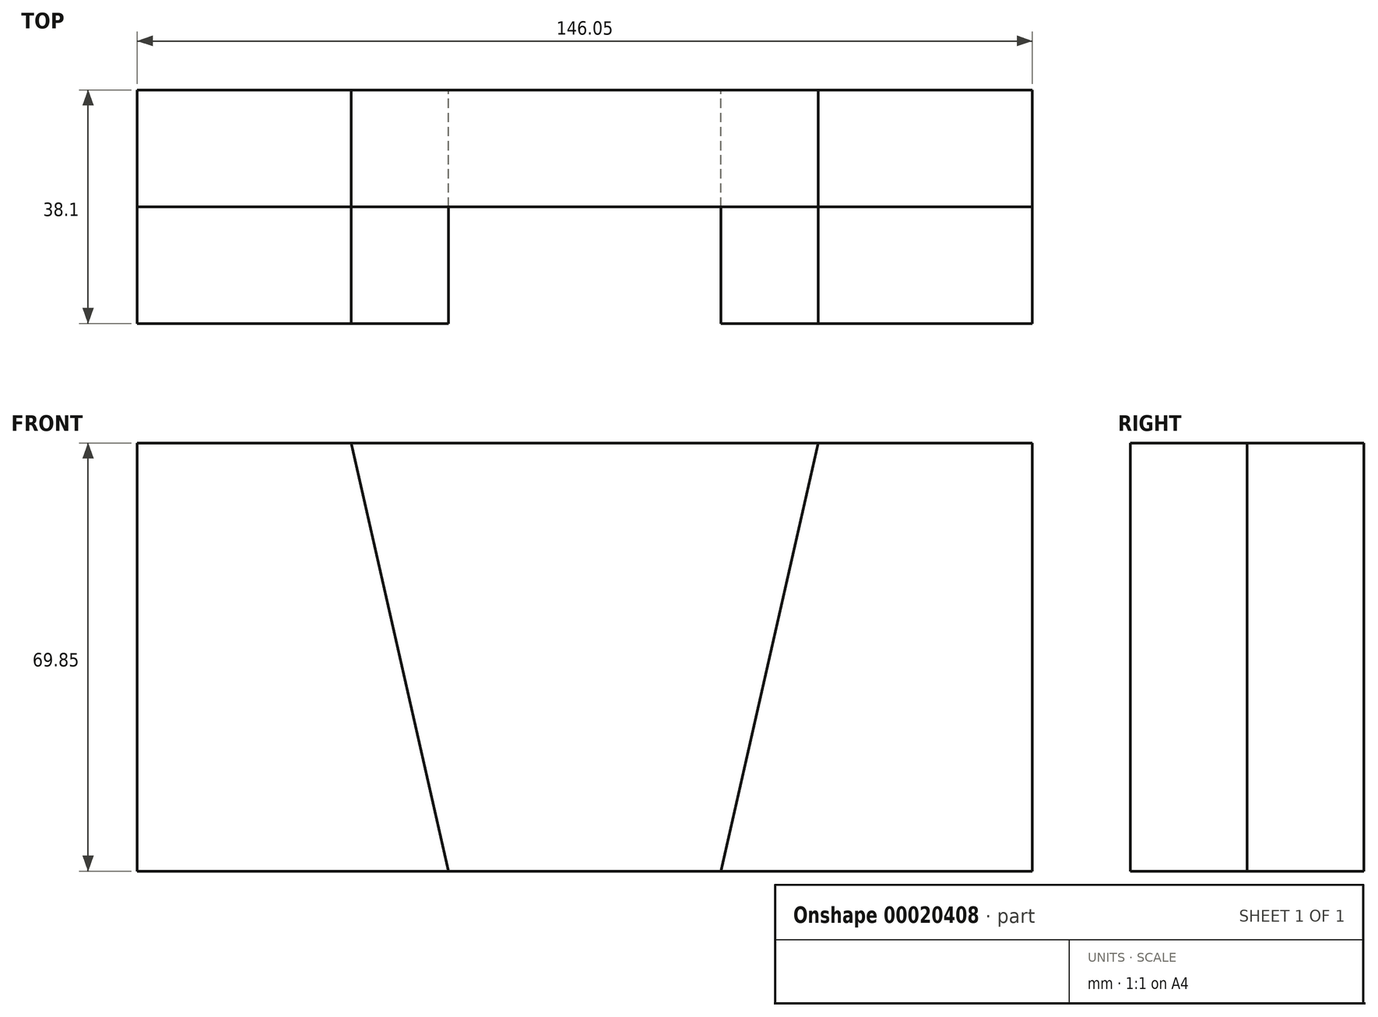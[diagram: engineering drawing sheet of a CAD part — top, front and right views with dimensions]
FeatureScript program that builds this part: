
annotation { "Feature Type Name" : "Feature", "Feature Type Description" : "" }
export const myFeature = defineFeature(function(context is Context, id is Id, definition is map)
    precondition{}
    {
        {
            var Q0;
            Q0=qCreatedBy(makeId("Front.planeOp"),FACE);
            var sketch = newSketch(context, id + "F0", { "sketchPlane" : qUnion([Q0])});
            skLineSegment(sketch, "E0.bottom", {"start": v(-72.73, 28.3) * mm, "end": v(73.32, 28.3) * mm});
            skLineSegment(sketch, "E0.top", {"start": v(-72.73, -41.55) * mm, "end": v(73.32, -41.55) * mm});
            skLineSegment(sketch, "E0.left", {"start": v(-72.73, 28.3) * mm, "end": v(-72.73, -41.55) * mm});
            skLineSegment(sketch, "E0.right", {"start": v(73.32, 28.3) * mm, "end": v(73.32, -41.55) * mm});
            skLineSegment(sketch, "E1", {"start": v(73.32, 28.3) * mm, "end": v(38.4, 28.3) * mm});
            skLineSegment(sketch, "E2", {"start": v(-72.73, 28.3) * mm, "end": v(-37.8, 28.3) * mm});
            skLineSegment(sketch, "E3", {"start": v(73.32, -41.55) * mm, "end": v(22.52, -41.55) * mm});
            skLineSegment(sketch, "E4", {"start": v(-72.73, -41.55) * mm, "end": v(-21.93, -41.55) * mm});
            skLineSegment(sketch, "E5", {"start": v(-37.8, 28.3) * mm, "end": v(-21.93, -41.55) * mm});
            skLineSegment(sketch, "E6", {"start": v(38.4, 28.3) * mm, "end": v(22.52, -41.55) * mm});
            skSolve(sketch);
        }
        {
            var Q0;
            Q0=makeQuery(id+"F0.imprint","IMPRINT",FACE,{"disambiguationData":[TD([[makeQuery(id+"F0.imprint","IMPRINT",EDGE,{"derivedFrom":sQuery(id+"F0.wireOp",EDGE,"E0.left")}),1.0]])]});
            var Q1;
            Q1=makeQuery(id+"F0.imprint","IMPRINT",FACE,{"disambiguationData":[TD([[makeQuery(id+"F0.imprint","IMPRINT",EDGE,{"derivedFrom":sQuery(id+"F0.wireOp",EDGE,"E0.right")}),-1.0]])]});
            extrude(context, id + "F1", {"entities" : qUnion([Q0, Q1]), "depth" : 38.1 * mm});
        }
        {
            var Q0;
            Q0 = qSketchRegion(id + "F0", true);
            extrude(context, id + "F2", {"entities" : qUnion([Q0]), "depth" : 19.05 * mm});
        }
    });
